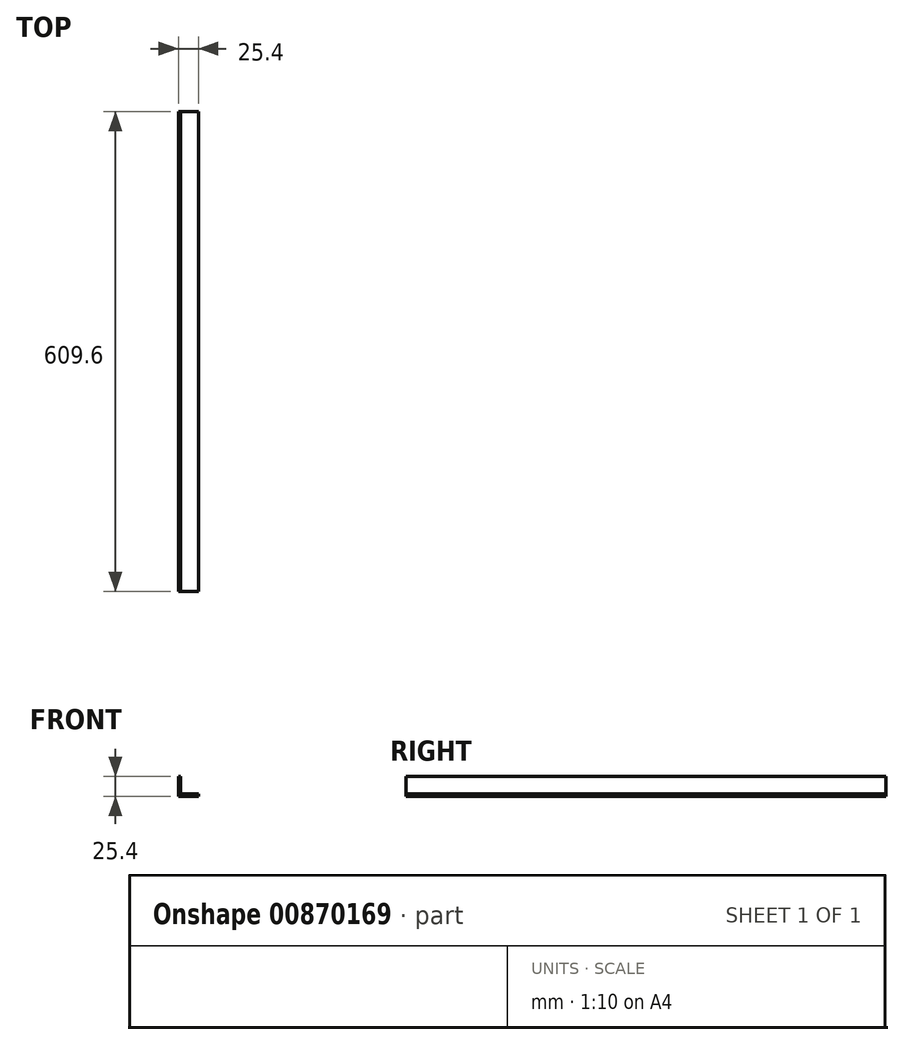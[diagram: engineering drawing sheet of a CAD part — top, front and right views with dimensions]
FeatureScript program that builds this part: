
annotation { "Feature Type Name" : "Feature", "Feature Type Description" : "" }
export const myFeature = defineFeature(function(context is Context, id is Id, definition is map)
    precondition{}
    {
        {
            var Q0;
            Q0=qCreatedBy(makeId("Front.planeOp"),FACE);
            var sketch = newSketch(context, id + "F0", { "sketchPlane" : qUnion([Q0])});
            skLineSegment(sketch, "E0.bottom", {"start": v(0, 25.4) * mm, "end": v(3.17, 25.4) * mm});
            skLineSegment(sketch, "E0.top", {"start": v(0, 0) * mm, "end": v(25.4, 0) * mm});
            skLineSegment(sketch, "E0.left", {"start": v(0, 25.4) * mm, "end": v(0, 0) * mm});
            skLineSegment(sketch, "E0.right", {"start": v(25.4, 3.18) * mm, "end": v(25.4, 0) * mm});
            skLineSegment(sketch, "E1.top", {"start": v(3.18, 3.17) * mm, "end": v(25.4, 3.17) * mm});
            skLineSegment(sketch, "E1.left", {"start": v(3.17, 25.4) * mm, "end": v(3.17, 3.18) * mm});
            skSolve(sketch);
        }
        {
            var Q0;
            Q0 = qSketchRegion(id + "F0", true);
            extrude(context, id + "F1", {"entities" : qUnion([Q0]), "oppositeDirection" : true, "depth" : 609.6 * mm, "offsetDistance" : 25.4 * mm});
        }
    });
